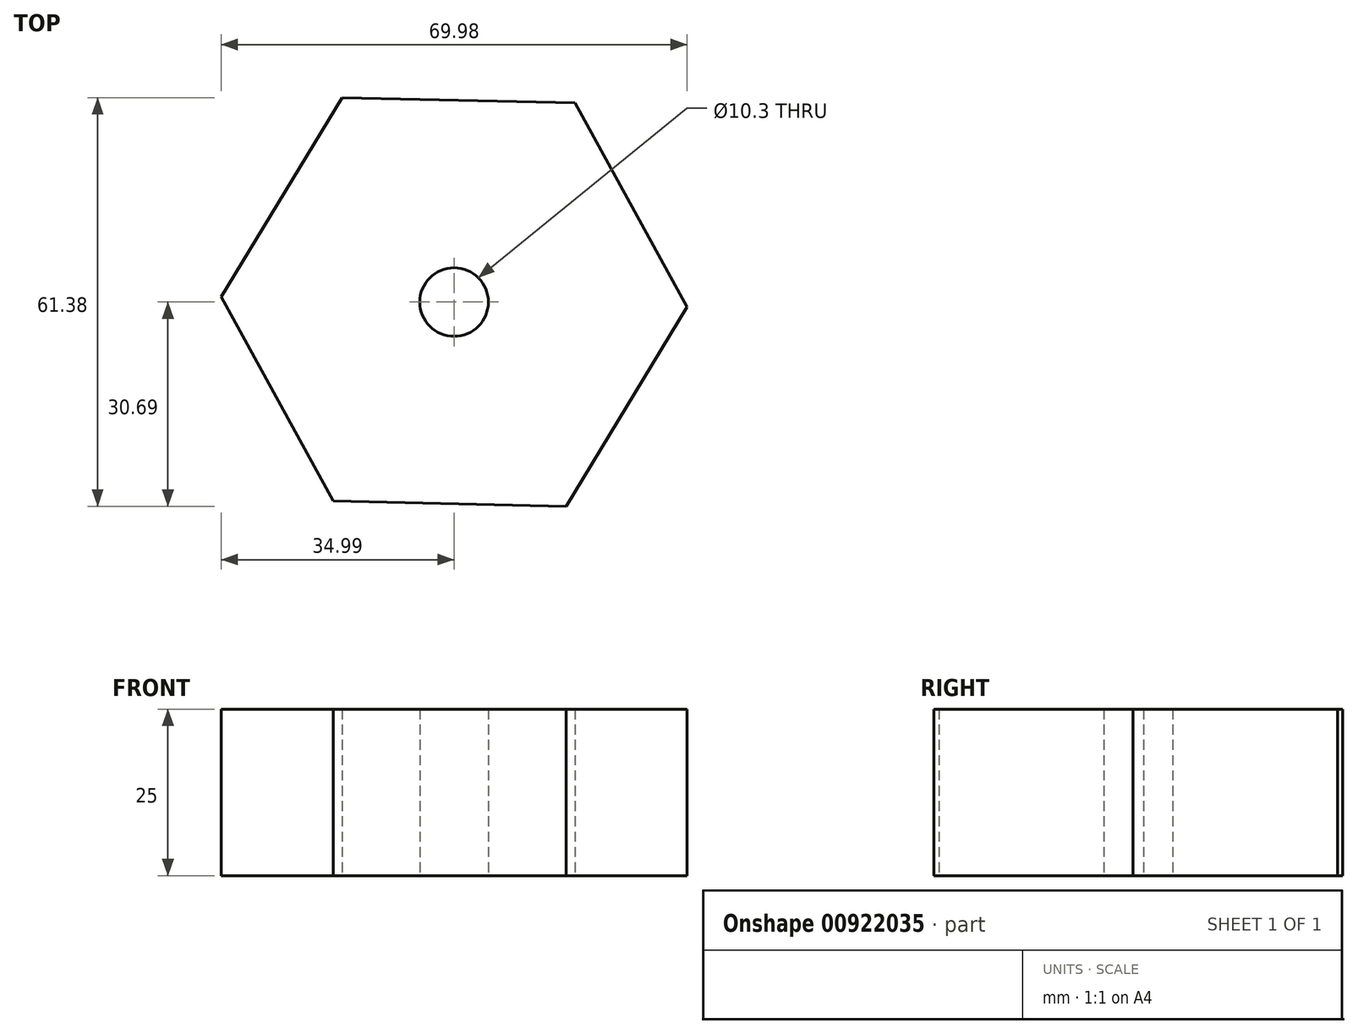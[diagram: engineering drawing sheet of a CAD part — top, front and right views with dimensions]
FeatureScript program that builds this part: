
annotation { "Feature Type Name" : "Feature", "Feature Type Description" : "" }
export const myFeature = defineFeature(function(context is Context, id is Id, definition is map)
    precondition{}
    {
        {
            var Q0;
            Q0=qCreatedBy(makeId("Top.planeOp"),FACE);
            var sketch = newSketch(context, id + "F0", { "sketchPlane" : qUnion([Q0])});
            skCircle(sketch, "E0.cCircle", {"center": v(0, 0) * mm, "radius": 30.31 * mm, "construction": true});
            skLineSegment(sketch, "E0.0", {"start": v(-35, 0.77) * mm, "end": v(-16.83, 30.69) * mm});
            skLineSegment(sketch, "E0.1", {"start": v(-16.83, 30.69) * mm, "end": v(18.16, 29.92) * mm});
            skLineSegment(sketch, "E0.2", {"start": v(18.16, 29.92) * mm, "end": v(35, -0.77) * mm});
            skLineSegment(sketch, "E0.3", {"start": v(35, -0.77) * mm, "end": v(16.83, -30.69) * mm});
            skLineSegment(sketch, "E0.4", {"start": v(16.83, -30.69) * mm, "end": v(-18.16, -29.92) * mm});
            skLineSegment(sketch, "E0.5", {"start": v(-18.16, -29.92) * mm, "end": v(-35, 0.77) * mm});
            skPoint(sketch, "E0.0.midPoint", {"position": v(-25.91, 15.73) * mm});
            skSolve(sketch);
        }
        {
            var Q0;
            Q0=makeQuery(id+"F0.imprint","IMPRINT",FACE,{"disambiguationData":[TD([[makeQuery(id+"F0.imprint","IMPRINT",EDGE,{"derivedFrom":sQuery(id+"F0.wireOp",EDGE,"E0.0")}),-1.0]])]});
            extrude(context, id + "F1", {"entities" : qUnion([Q0]), "depth" : 25 * mm, "offsetDistance" : 25 * mm});
        }
        {
            var Q0;
            Q0=makeQuery(id+"F1.opExtrude","CAP_FACE",FACE,{"disambiguationData":[OSD([sQuery(id+"F0.wireOp",EDGE,"E0.0"),sQuery(id+"F0.wireOp",EDGE,"E0.1"),sQuery(id+"F0.wireOp",EDGE,"E0.2"),sQuery(id+"F0.wireOp",EDGE,"E0.3"),sQuery(id+"F0.wireOp",EDGE,"E0.4"),sQuery(id+"F0.wireOp",EDGE,"E0.5")])],"isStart":true});
            var sketch = newSketch(context, id + "F2", { "sketchPlane" : qUnion([Q0])});
            skCircle(sketch, "E1", {"center": v(0, 0) * mm, "radius": 7.06 * mm});
            skSolve(sketch);
        }
        {
            var Q0;
            Q0=sQuery(id+"F2.wireOp",VERTEX,"E1.center");
            var Q1;
            Q1=makeQuery(id+"F1.opExtrude","SWEPT_BODY",BODY,{"disambiguationData":[OSD([sQuery(id+"F0.wireOp",EDGE,"E0.0"),sQuery(id+"F0.wireOp",EDGE,"E0.1"),sQuery(id+"F0.wireOp",EDGE,"E0.2"),sQuery(id+"F0.wireOp",EDGE,"E0.3"),sQuery(id+"F0.wireOp",EDGE,"E0.4"),sQuery(id+"F0.wireOp",EDGE,"E0.5")])]});
            hole(context, id + "F3", {"style" : HoleStyle.SIMPLE, "endStyle" : HoleEndStyle.BLIND, "standardTappedOrClearance" : lookupTablePath({ "standard" : "ISO", "engagement" : "75%", "pitch" : "1.75 mm", "size" : "M12", "type" : "Tapped" }), "standardBlindInLast" : lookupTablePath({ "standard" : "ISO", "engagement" : "75%", "pitch" : "1.75 mm", "size" : "M12", "type" : "Tapped" }), "holeDiameter" : 10.3 * mm, "majorDiameter" : 12 * mm, "showTappedDepth" : true, "holeDepth" : 35.25 * mm, "isTappedThrough" : true, "tappedDepth" : 30 * mm, "tapClearance" : 3, "locations" : qUnion([Q0]), "scope" : qUnion([Q1])});
        }
    });
